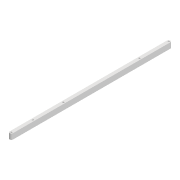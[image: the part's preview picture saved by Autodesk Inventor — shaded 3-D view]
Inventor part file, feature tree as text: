
AUTODESK INVENTOR PART (.ipt)
format: ipt  version: 2022 (Build 260153000, 153)  size: 98,304 bytes
history: native  units: mm
features: extrude x1, sketch x1
ambient origin geometry x8: Origin, YZ Plane, XZ Plane, XY Plane, X Axis, Y Axis, Z Axis, Center Point
bodies: Solid1 (feature_tree)
feature tree (2):
  extrude  "Extrusion1"  Depth=287.501mm
  sketch  "Sketch1"  dims[d0=6.0mm d1=287.501mm d2=3.0mm d3=3.0mm d4=10.0mm d5=0.0mm d14=3.0mm d15=39.171mm d16=3.0mm d17=94.738mm d18=3.0mm d19=233.822mm]
